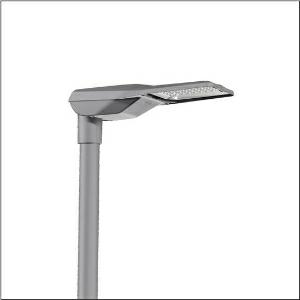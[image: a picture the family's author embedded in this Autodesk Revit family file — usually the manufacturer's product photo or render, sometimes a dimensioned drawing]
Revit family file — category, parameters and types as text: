
# Revit family: streetlight_sl_21_mini___p1_0a_5xe6a43a08gb_8ec3
name_source: partatom
category: Lighting Fixtures
units: mm (PartAtom-declared; Revit-internal decimal feet)

## family parameters
Cut with Voids When Loaded = No
Host = Face
Light Source = No
Part Type = Normal
Room Calculation Point = No
Round Connector Dimension = Use Diameter
Shared = No

## types (1)
- --- (1 x LED, 6180 lm, 40.4 W, 4000K)
    Apparent Load = 40 VA
    CIE Flux Codes = 21 50 90 100 100
    Color Rendering = 70
    Color Temperature = 4000K
    Default Elevation = 1800 mm
    Description = Streetlight SL 21 mini, mast luminaire, primary light control with lens, of PMMA, primary optical cover: cover, of toughened safety glass, transparent, light distribution: P1.0a, light emission: direct distribution, primary light characteristic: asymmetric, installation type: post-top, side-entry, LED, 3G 1.5mm², High Power LED, rated luminous flux: 6.180lm, luminous efficacy: 153lm/W, light colour: 740, colour temperature: 4000K, control gear: Easy, control: overheat protection, constant luminous flux control, time-dependent luminous flux control, flexible luminous flux parameterisation, mains connection: 230..240V, AC, 50/60Hz, connection cable pre-assembled, cable length: 6,5m, wiring characteristics: H07RN-F, start of lifetime: 40W, end of service life: 41W, reduction: 19W, luminaire housing, of diecast aluminium, powder-coated, Siteco® metallic grey (DB 702S), corrosivity category C5 mid according to DIN EN ISO 12944, please order mast flange separately, inclination adjustable: 0°, 5°, 10°, 15°, sealing non-destructively replaceable, multi-level sealing system, length: 628mm, width: 235mm, height: 110mm, mast flange for spigot size: 42mm (side-entry): 5XC10008XM4, 60/48mm (side-entry/post-top): 5XC10108XM2, 76/60mm (side-entry/post-top): 5XC10108XM1, mounting height: 4..8m, protection rating (complete): IP66, insulation class (complete): insulation class II (safety insulation), certification: CE, ENEC, ENEC+, VDE, impact resistance: IK10, permissible operating ambient temperature for outdoor applications: -40..+50°C, standard-compliant lighting for roads and squares, packaging unit: 1 piece

Light Distribution: P1.0a
    Height = 110 mm
    Lamp = 1 x LED
    Lamp Light Flux = 6180 lm
    Lamp Power = 40.4 W
    Lamp count = 1
    Length = 625 mm
    Luminous efficacy = 153 lm/W
    Manufacturer = Siteco
    ModVariant = No
    Model = 5XE6A43A08GB
    Number of Poles = 1
    OnlyDefault = Yes
    Power Factor = 1
    Product Name = Streetlight SL 21 mini | P1.0a
    Product group = mast luminaire | pylon top
    ProductGroupID = 6100
    Protection Class = Protection class II
    Protection Degree = IP 66
    RLX_Detail_Level = 1
    RLX_Emergency_Light_Flux = 0 lm
    RLX_Emergency_Type = 0
    RLX_Emergency_Type_DB = No
    RlxData = <blob elided: 37113 chars, md5=8d28def2>
    Socket = socket
    Standby Power = 0 W
    System Light Flux = 6180 lm
    System Power = 40 W
    Type Comments = factory setting: luminous flux: 100 % | Output Level: 100 % | 812 mA
    Type Image = l_1003519.jpg
    URL = http://relux.com
    VarID = @adj_186370
    Voltage = 0 V
    Weight = 0.00 kg
    Width = 234 mm

## geometry (parser evidence)
native form markers: Blend x4, Sweep x10
no freeform markers — native parametric forms only
